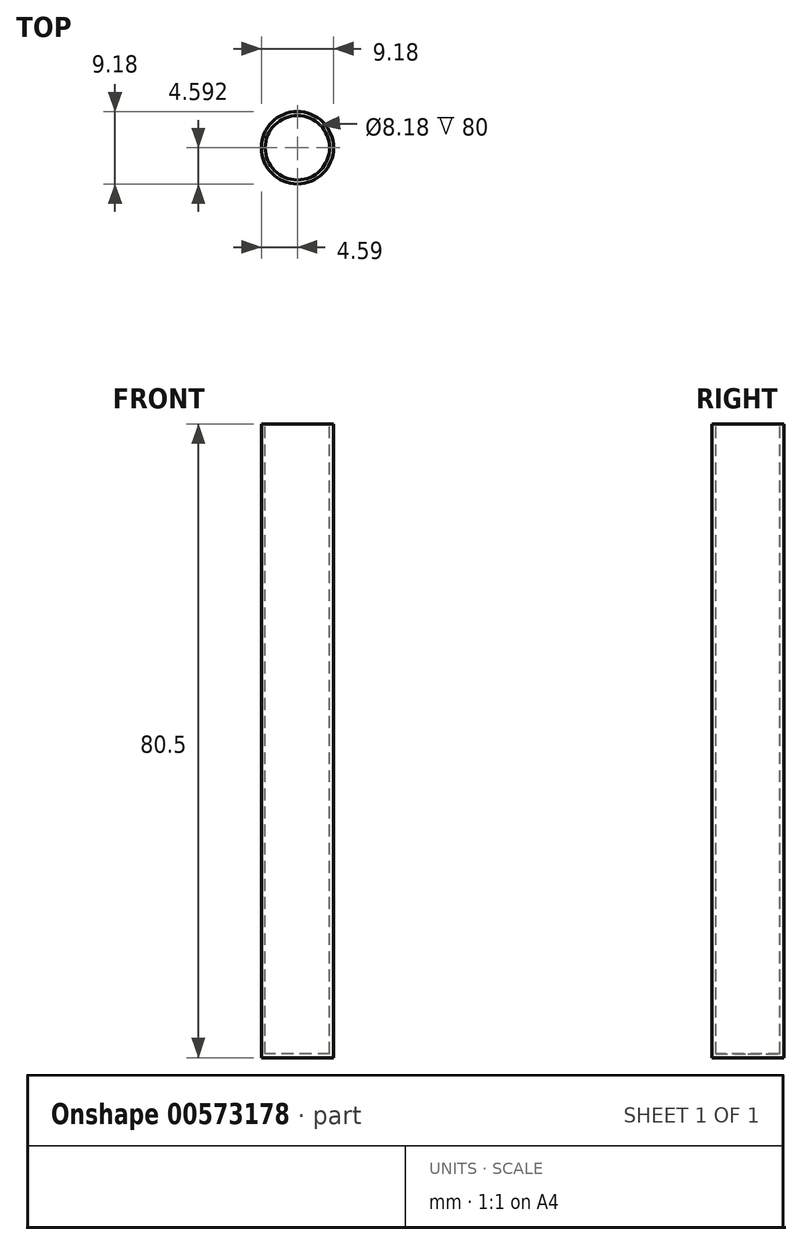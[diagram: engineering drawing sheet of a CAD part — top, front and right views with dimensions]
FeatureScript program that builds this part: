
annotation { "Feature Type Name" : "Feature", "Feature Type Description" : "" }
export const myFeature = defineFeature(function(context is Context, id is Id, definition is map)
    precondition{}
    {
        {
            var Q0;
            Q0=qCreatedBy(makeId("Top.planeOp"),FACE);
            var sketch = newSketch(context, id + "F0", { "sketchPlane" : qUnion([Q0])});
            skCircle(sketch, "E0", {"center": v(0, 7.53) * mm, "radius": 4.1 * mm});
            skSolve(sketch);
        }
        {
            var Q0;
            Q0=makeQuery(id+"F0.imprint","IMPRINT",FACE,{"disambiguationData":[TD([[makeQuery(id+"F0.imprint","IMPRINT",EDGE,{"derivedFrom":sQuery(id+"F0.wireOp",EDGE,"E0")}),1.0]])]});
            extrude(context, id + "F1", {"entities" : qUnion([Q0]), "oppositeDirection" : true, "depth" : 80 * mm, "offsetDistance" : 25 * mm});
        }
        {
            var Q0;
            Q0=makeQuery(id+"F1.opExtrude","CAP_FACE",FACE,{"disambiguationData":[OSD([sQuery(id+"F0.wireOp",EDGE,"E0")])],"isStart":true});
            var Q1;
            Q1=makeQuery(id+"F1.opExtrude","SWEPT_BODY",BODY,{"disambiguationData":[OSD([sQuery(id+"F0.wireOp",EDGE,"E0")])]});
            shell(context, id + "F2", {"entities" : qUnion([Q0]), "parts" : qUnion([Q1]), "thickness" : 0.5 * mm, "oppositeDirection" : true});
        }
    });
